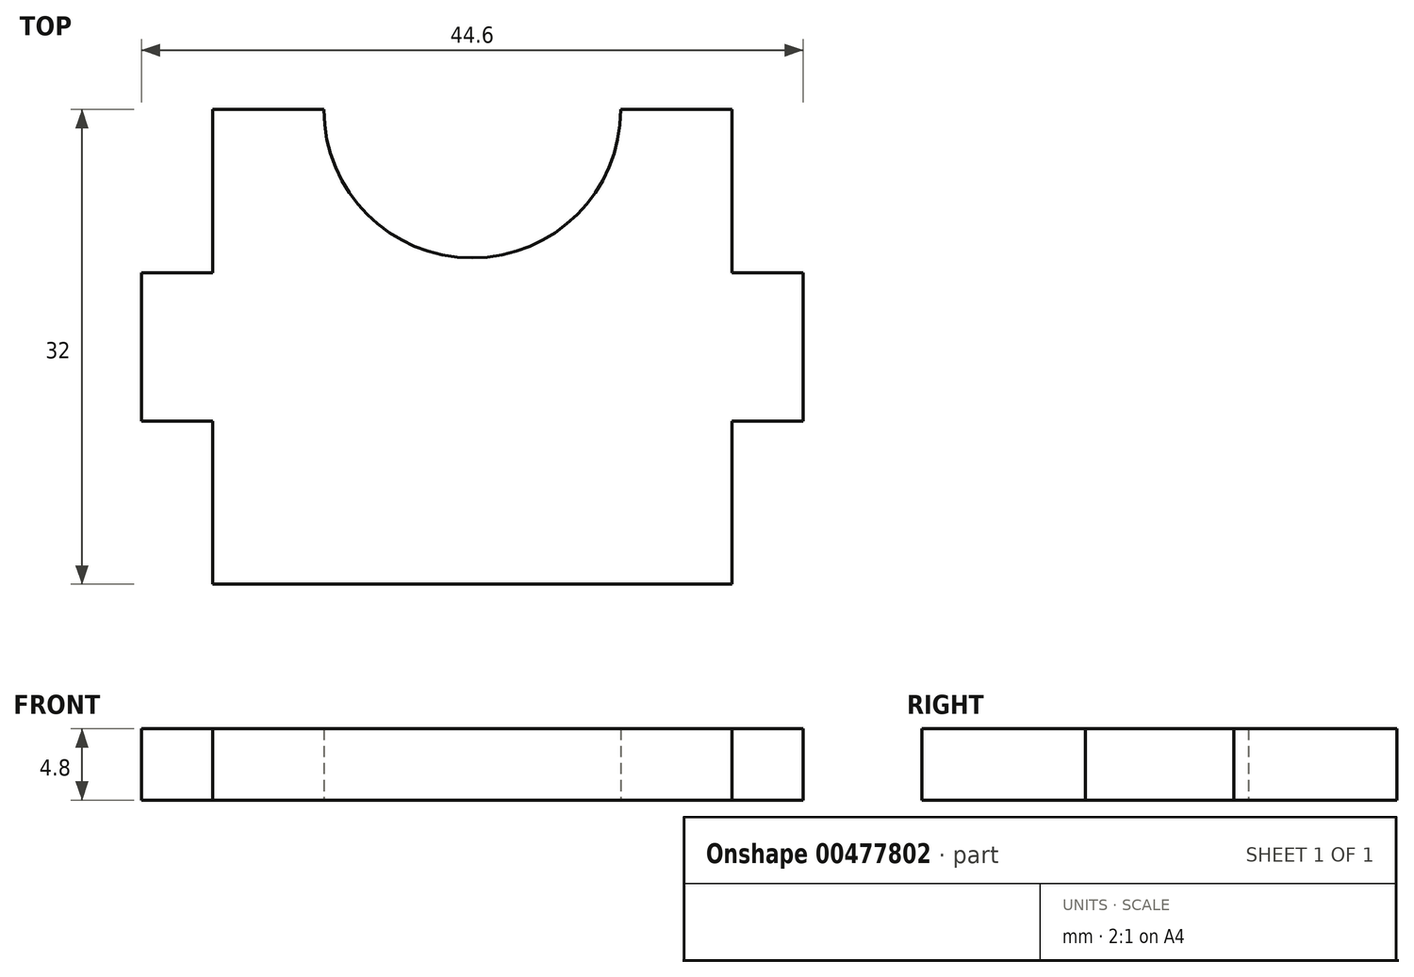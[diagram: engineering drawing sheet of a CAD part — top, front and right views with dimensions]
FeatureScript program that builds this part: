
annotation { "Feature Type Name" : "Feature", "Feature Type Description" : "" }
export const myFeature = defineFeature(function(context is Context, id is Id, definition is map)
    precondition{}
    {
        {
            var Q0;
            Q0=qCreatedBy(makeId("Top.planeOp"),FACE);
            var sketch = newSketch(context, id + "F0", { "sketchPlane" : qUnion([Q0])});
            skLineSegment(sketch, "E0.bottom", {"start": v(0, 0) * mm, "end": v(35, 0) * mm});
            skLineSegment(sketch, "E0.top", {"start": v(0, 32) * mm, "end": v(35, 32) * mm});
            skLineSegment(sketch, "E0.left", {"start": v(0, 0) * mm, "end": v(0, 32) * mm});
            skLineSegment(sketch, "E0.right", {"start": v(35, 0) * mm, "end": v(35, 32) * mm});
            skLineSegment(sketch, "E1.bottom", {"start": v(0, 21) * mm, "end": v(-4.8, 21) * mm});
            skLineSegment(sketch, "E1.top", {"start": v(0, 11) * mm, "end": v(-4.8, 11) * mm});
            skLineSegment(sketch, "E1.left", {"start": v(0, 21) * mm, "end": v(0, 11) * mm});
            skLineSegment(sketch, "E1.right", {"start": v(-4.8, 21) * mm, "end": v(-4.8, 11) * mm});
            skLineSegment(sketch, "E2.bottom", {"start": v(35, 21) * mm, "end": v(39.8, 21) * mm});
            skLineSegment(sketch, "E2.top", {"start": v(35, 11) * mm, "end": v(39.8, 11) * mm});
            skLineSegment(sketch, "E2.left", {"start": v(35, 21) * mm, "end": v(35, 11) * mm});
            skLineSegment(sketch, "E2.right", {"start": v(39.8, 21) * mm, "end": v(39.8, 11) * mm});
            skArc(sketch, "E3", {"start": v(7.5, 32) * mm, "mid": v(17.5, 22) * mm, "end": v(27.5, 32) * mm});
            skSolve(sketch);
        }
        {
            var Q0;
            {var subQ1=sQuery(id+"F0.wireOp",EDGE,"E0.bottom");Q0=makeQuery(id+"F0.imprint","IMPRINT",FACE,{"disambiguationData":[TD([[makeQuery(id+"F0.imprint","IMPRINT",EDGE,{"derivedFrom":subQ1}),1.0]])]});}
            var Q1;
            Q1=makeQuery(id+"F0.imprint","IMPRINT",FACE,{"disambiguationData":[TD([[makeQuery(id+"F0.imprint","IMPRINT",EDGE,{"derivedFrom":sQuery(id+"F0.wireOp",EDGE,"E1.bottom")}),1.0]])]});
            var Q2;
            Q2=makeQuery(id+"F0.imprint","IMPRINT",FACE,{"disambiguationData":[TD([[makeQuery(id+"F0.imprint","IMPRINT",EDGE,{"derivedFrom":sQuery(id+"F0.wireOp",EDGE,"E2.bottom")}),-1.0]])]});
            extrude(context, id + "F1", {"entities" : qUnion([Q0, Q1, Q2]), "depth" : 4.8 * mm});
        }
    });
